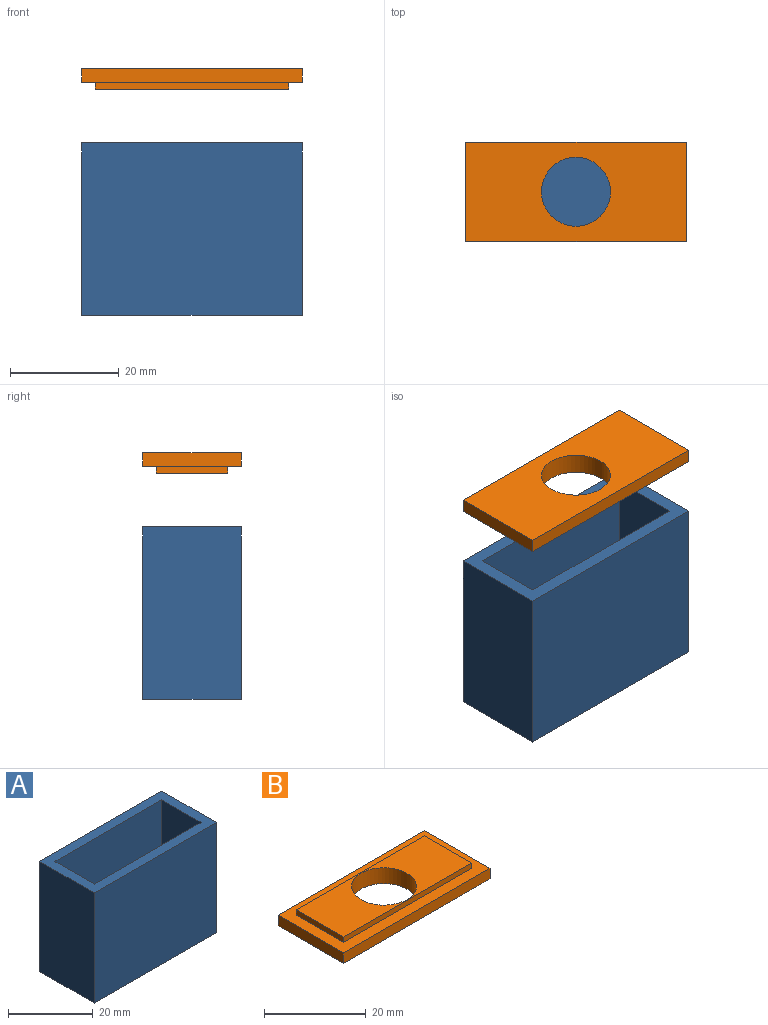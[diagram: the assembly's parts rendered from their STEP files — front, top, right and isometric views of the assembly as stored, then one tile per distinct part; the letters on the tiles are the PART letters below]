
ASSEMBLY  parts=2 mates=1
PART A: 11 faces, bbox 40.6x18.2x31.8 mm
  f0: plane 40.64x18.16mm, normal (0,0,1), area 272.9mm2, adj f1,f2,f3,f4,f6,f7,f8,f9
  f1: plane 40.64x31.75mm, normal (0,-1,0), area 1290.3mm2, adj f0,f2,f4,f5
  f2: plane 31.75x18.16mm, normal (1,0,0), area 576.6mm2, adj f0,f1,f3,f5
  f3: plane 40.64x31.75mm, normal (0,1,0), area 1290.3mm2, adj f0,f2,f4,f5
  f4: plane 31.75x18.16mm, normal (-1,0,0), area 576.6mm2, adj f0,f1,f3,f5
  f5: plane 40.64x18.16mm, normal (0,0,-1), area 738.1mm2, adj f1,f2,f3,f4
  f6: plane 35.56x29.21mm, normal (0,1,0), area 1038.7mm2, adj f0,f7,f9,f10
  f7: plane 29.21x13.08mm, normal (-1,0,0), area 382.1mm2, adj f0,f6,f8,f10
  f8: plane 35.56x29.21mm, normal (0,-1,0), area 1038.7mm2, adj f0,f7,f9,f10
  f9: plane 29.21x13.08mm, normal (1,0,0), area 382.1mm2, adj f0,f6,f8,f10
  f10: plane 35.56x13.08mm, normal (0,0,1), area 465.2mm2, adj f6,f7,f8,f9
PART B: 12 faces, bbox 40.6x18.2x3.8 mm
  f0: plane 40.64x2.54mm, normal (0,1,0), area 103.2mm2, adj f1,f3,f4,f5
  f1: plane 18.16x2.54mm, normal (-1,0,0), area 46.1mm2, adj f0,f2,f4,f5
  f2: plane 40.64x2.54mm, normal (0,-1,0), area 103.2mm2, adj f1,f3,f4,f5
  f3: plane 18.16x2.54mm, normal (1,0,0), area 46.1mm2, adj f0,f2,f4,f5
  f4: plane 40.64x18.16mm, normal (0,0,1), area 272.9mm2, adj f0,f1,f2,f3,f6,f7,f8,f9
  f5: plane 40.64x18.16mm, normal (0,0,-1), area 611.4mm2, adj f0,f1,f2,f3,f10
  f6: plane 13.08x1.27mm, normal (1,0,0), area 16.6mm2, adj f4,f7,f9,f11
  f7: plane 35.56x1.27mm, normal (0,-1,0), area 45.2mm2, adj f4,f6,f8,f11
  f8: plane 13.08x1.27mm, normal (-1,0,0), area 16.6mm2, adj f4,f7,f9,f11
  f9: plane 35.56x1.27mm, normal (0,1,0), area 45.2mm2, adj f4,f6,f8,f11
  f10: cylinder r=6.35mm len=12.7mm, axis (0,0,-1), area 152mm2, adj f5,f11
  f11: plane 35.56x13.08mm, normal (0,0,1), area 338.5mm2, adj f6,f7,f8,f9,f10
PLACE A rot(axis=(0.03,-1,0.02),0deg) t=(-7.9,-10.73,-10.2)mm
PLACE B rot(axis=(0,1,0),180deg) t=(38.34,-10.73,35.25)mm
MATE slider B.f10 <-> A.f5  axis (0,0,1) through (-7.9,-10.73,35.25)mm
